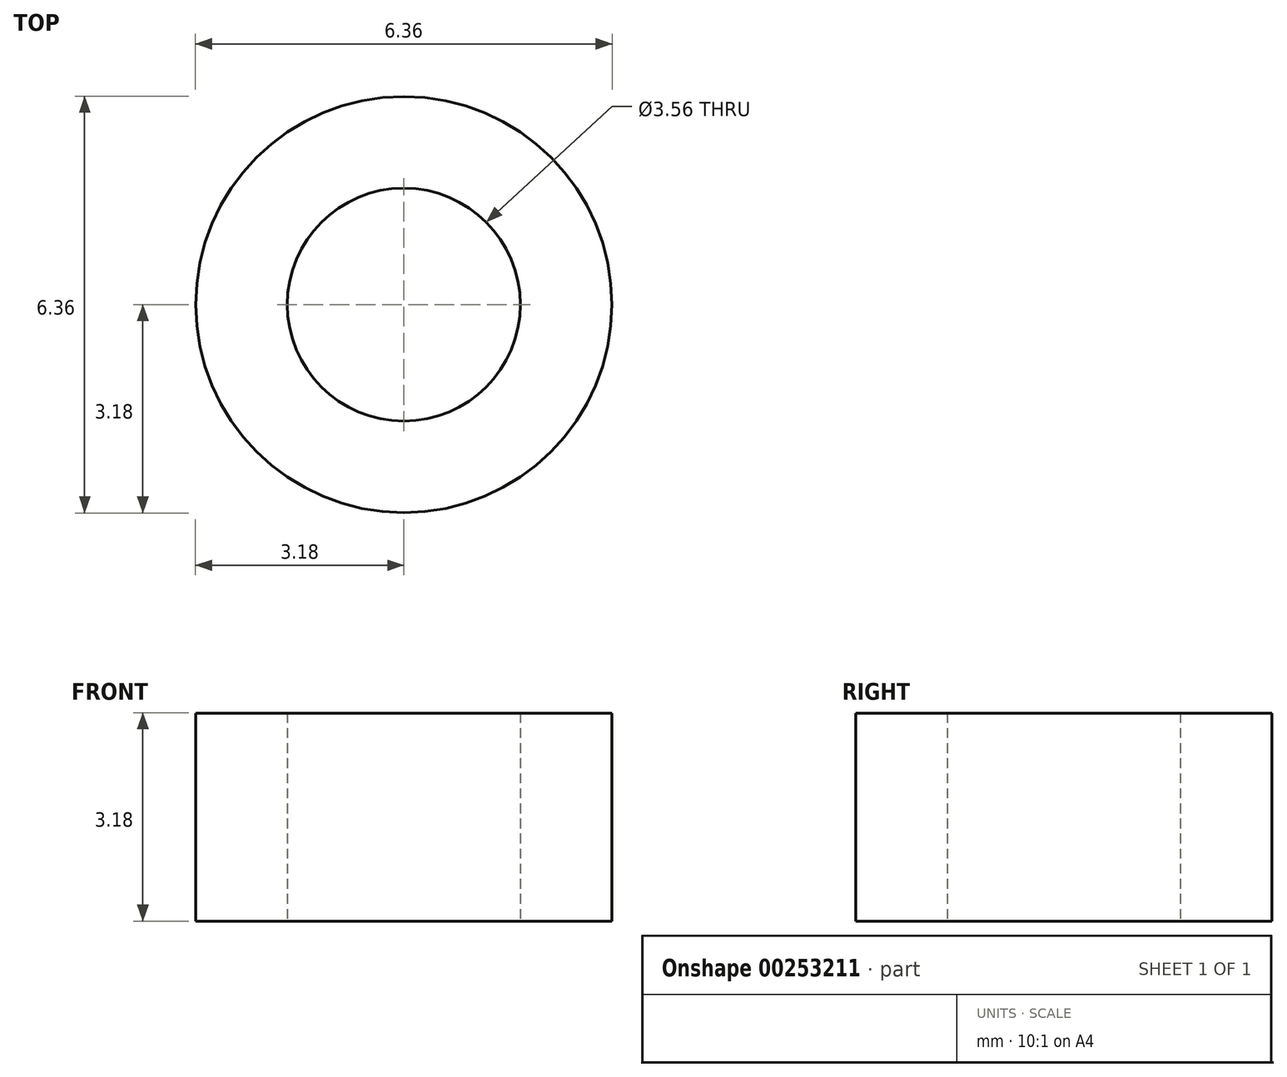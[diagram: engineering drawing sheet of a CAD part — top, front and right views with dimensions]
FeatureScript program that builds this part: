
annotation { "Feature Type Name" : "Feature", "Feature Type Description" : "" }
export const myFeature = defineFeature(function(context is Context, id is Id, definition is map)
    precondition{}
    {
        {
            var Q0;
            Q0=qCreatedBy(makeId("Top.planeOp"),FACE);
            var sketch = newSketch(context, id + "F0", { "sketchPlane" : qUnion([Q0])});
            skCircle(sketch, "E0", {"center": v(0, 0) * mm, "radius": 1.78 * mm});
            skCircle(sketch, "E1", {"center": v(0, 0) * mm, "radius": 3.18 * mm});
            skSolve(sketch);
        }
        {
            var Q0;
            Q0 = qSketchRegion(id + "F0", true);
            extrude(context, id + "F1", {"entities" : qUnion([Q0]), "depth" : 3.17 * mm});
        }
    });
